# Revit family: РОСМА_МанометрКоррозионностойкийИзмеренияНизкДавлГазов
name_source: partatom
category: Арматура трубопроводов
revit_build: Autodesk Revit 2018 (Build: 20180423_1000(x64)
units: mm (PartAtom-declared; Revit-internal decimal feet)

## family parameters
Всегда вертикально = Да
На основе рабочей плоскости = Нет
Общий = Нет
При загрузке вырезать с полостями = Нет
Размер круглого соединителя = Использовать диаметр
Тип детали = Вставляется

## types (2) — shared parameters
ADSK_Единица измерения = шт.
ADSK_Количество = 1
DN = 15.00 мм
Table = спец_коррозионностойкий для измерения низких давлений газов
Table_2 = размеры_коррозионностойкий для измерения низких давлений газов
URL = https://rosma.spb.ru
Группа модели = Оборудование
Давление01 = ‎ : КМ 0…2.5кПа
Давление02 = ‎ : КМ 0…4кПа
Давление03 = ‎ : КМ 0…6кПа
Давление04 = ‎ : КМ 0…10кПа
Давление05 = ‎ : КМ 0…16кПа
Давление06 = ‎ : КМ 0…25кПа
Давление07 = ‎ : КМ 0…40кПа
Давление08 = ‎ : КМ 0…60кПа
Давление09 = ‎ : КМВ -1…1.5кПа
Давление10 = ‎ : КМВ -1…3кПа
Изготовитель = ЗАО "РОСМА"
Класс точности = 1,5
Климатическое исполнение = Группа Д2 по ГОСТ Р 52931; климатическое исполнение УХЛ категории 1.1 по ГОСТ 15150
Межповерочный интервал = 2 года
Описание = Тип КМВ, Кс. Манометр для измерения давления сухих, газообразных агрессивных сред.
Радиальное присоединение = Да
Техническая документация = ТУ 4212-001-4719015564-2008; ГОСТ 2405–88
лого_задн_стенка = Да

## type names (no varying parameters)
- 22
- 32

note: column(s) folded — value = type name in every type: Исполнение
